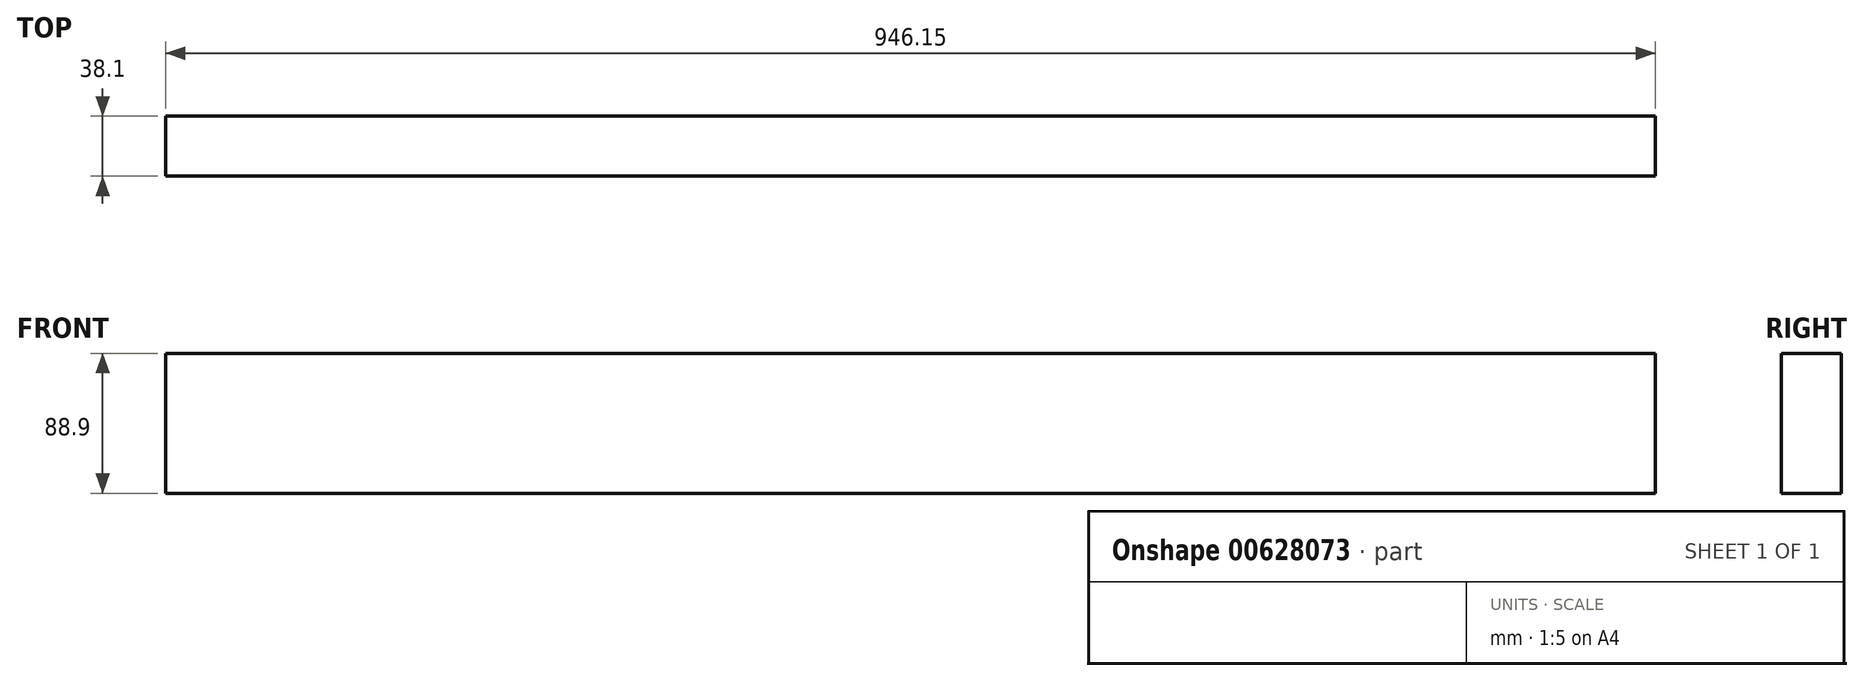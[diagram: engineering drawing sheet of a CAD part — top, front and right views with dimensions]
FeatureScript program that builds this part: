
annotation { "Feature Type Name" : "Feature", "Feature Type Description" : "" }
export const myFeature = defineFeature(function(context is Context, id is Id, definition is map)
    precondition{}
    {
        {
            var Q0;
            Q0=qCreatedBy(makeId("Front.planeOp"),FACE);
            var sketch = newSketch(context, id + "F0", { "sketchPlane" : qUnion([Q0])});
            skLineSegment(sketch, "E0.bottom", {"start": v(-546.3, 0) * mm, "end": v(399.85, 0) * mm});
            skLineSegment(sketch, "E0.top", {"start": v(-546.3, -88.9) * mm, "end": v(399.85, -88.9) * mm});
            skLineSegment(sketch, "E0.left", {"start": v(-546.3, 0) * mm, "end": v(-546.3, -88.9) * mm});
            skLineSegment(sketch, "E0.right", {"start": v(399.85, 0) * mm, "end": v(399.85, -88.9) * mm});
            skSolve(sketch);
        }
        {
            var Q0;
            Q0 = qSketchRegion(id + "F0", true);
            extrude(context, id + "F1", {"entities" : qUnion([Q0]), "depth" : 38.1 * mm, "offsetDistance" : 25.4 * mm});
        }
    });
